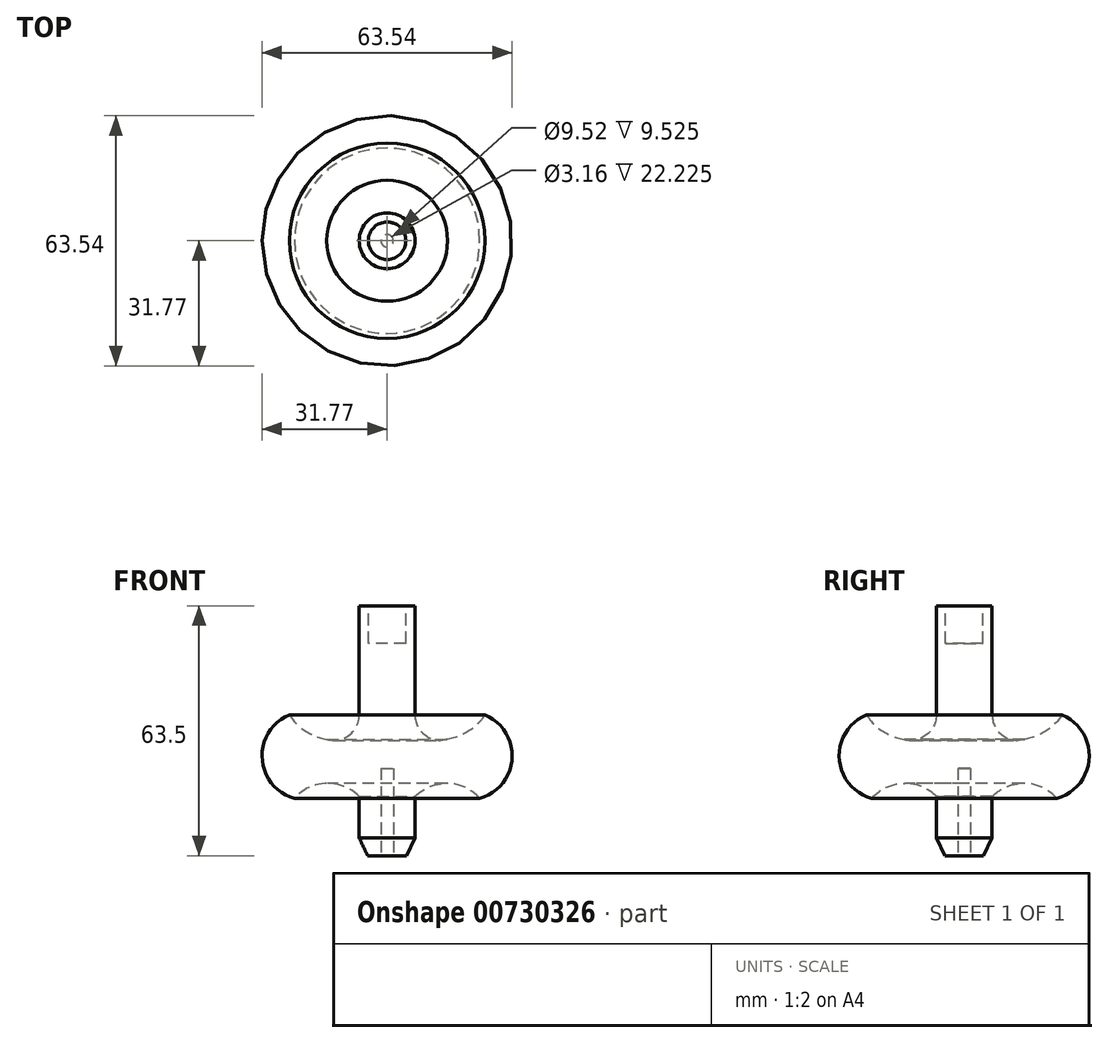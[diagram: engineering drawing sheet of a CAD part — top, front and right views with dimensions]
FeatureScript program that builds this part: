
annotation { "Feature Type Name" : "Feature", "Feature Type Description" : "" }
export const myFeature = defineFeature(function(context is Context, id is Id, definition is map)
    precondition{}
    {
        {
            var Q0;
            Q0=qCreatedBy(makeId("Front.planeOp"),FACE);
            var sketch = newSketch(context, id + "F0", { "sketchPlane" : qUnion([Q0])});
            skLineSegment(sketch, "E0", {"start": v(0, -24.54) * mm, "end": v(4.92, -24.54) * mm});
            skLineSegment(sketch, "E1", {"start": v(4.92, -24.54) * mm, "end": v(7.1, -20.04) * mm});
            skLineSegment(sketch, "E2", {"start": v(7.1, -20.04) * mm, "end": v(7.1, -9.5) * mm});
            skLineSegment(sketch, "E3", {"start": v(0, -24.54) * mm, "end": v(0, 38.96) * mm});
            skLineSegment(sketch, "E4", {"start": v(7.1, 11.28) * mm, "end": v(7.1, 38.96) * mm});
            skLineSegment(sketch, "E5", {"start": v(7.1, 38.96) * mm, "end": v(0, 38.96) * mm});
            skArc(sketch, "E6", {"start": v(23.52, -9.96) * mm, "mid": v(15.4, -6.12) * mm, "end": v(7.1, -9.5) * mm});
            skPoint(sketch, "E7", {"position": v(31.75, -27.48) * mm});
            skArc(sketch, "E8", {"start": v(23.52, -9.96) * mm, "mid": v(31.75, 0.2) * mm, "end": v(24.82, 11.28) * mm});
            skPoint(sketch, "E9", {"position": v(31.75, 1.57) * mm});
            skPoint(sketch, "E9.positionSnap0", {"position": v(31.75, 0.2) * mm});
            skArc(sketch, "E10", {"start": v(7.1, 11.28) * mm, "mid": v(9.68, 6.1) * mm, "end": v(15.37, 5.07) * mm});
            skArc(sketch, "E11", {"start": v(15.37, 5.07) * mm, "mid": v(20.77, 7.15) * mm, "end": v(24.82, 11.28) * mm});
            skSolve(sketch);
        }
        {
            var Q0;
            Q0=makeQuery(id+"F0.imprint","IMPRINT",FACE,{"disambiguationData":[TD([[makeQuery(id+"F0.imprint","IMPRINT",EDGE,{"derivedFrom":sQuery(id+"F0.wireOp",EDGE,"E0")}),1.0]])]});
            var Q1;
            Q1=sQuery(id+"F0.wireOp",EDGE,"E3");
            revolve(context, id + "F1", {"surfaceOperationType" : NewSurfaceOperationType.NEW, "entities" : qUnion([Q0]), "axis" : qUnion([Q1]), "revolveType" : RevolveType.FULL});
        }
        {
            var Q0;
            Q0=makeQuery(id+"F1.opRevolve","SWEPT_FACE",FACE,{"disambiguationData":[OSD([sQuery(id+"F0.wireOp",EDGE,"E5")])]});
            var sketch = newSketch(context, id + "F2", { "sketchPlane" : qUnion([Q0])});
            skCircle(sketch, "E12", {"center": v(0, 0) * mm, "radius": 4.76 * mm});
            skSolve(sketch);
        }
        {
            var Q0;
            Q0=makeQuery(id+"F2.imprint","IMPRINT",FACE,{"disambiguationData":[TD([[makeQuery(id+"F2.imprint","IMPRINT",EDGE,{"derivedFrom":sQuery(id+"F2.wireOp",EDGE,"E12")}),1.0]])]});
            extrude(context, id + "F3", {"entities" : qUnion([Q0]), "operationType" : NewBodyOperationType.REMOVE, "oppositeDirection" : true, "depth" : 9.52 * mm, "offsetDistance" : 25.4 * mm});
        }
        {
            var Q0;
            Q0=makeQuery(id+"F1.opRevolve","SWEPT_FACE",FACE,{"disambiguationData":[OSD([sQuery(id+"F0.wireOp",EDGE,"E0")])]});
            var sketch = newSketch(context, id + "F4", { "sketchPlane" : qUnion([Q0])});
            skCircle(sketch, "E13", {"center": v(0, 0) * mm, "radius": 1.58 * mm});
            skSolve(sketch);
        }
        {
            var Q0;
            Q0=makeQuery(id+"F4.imprint","IMPRINT",FACE,{"disambiguationData":[TD([[makeQuery(id+"F4.imprint","IMPRINT",EDGE,{"derivedFrom":sQuery(id+"F4.wireOp",EDGE,"E13")}),1.0]])]});
            extrude(context, id + "F5", {"entities" : qUnion([Q0]), "operationType" : NewBodyOperationType.REMOVE, "oppositeDirection" : true, "depth" : 22.22 * mm, "offsetDistance" : 25.4 * mm});
        }
    });
